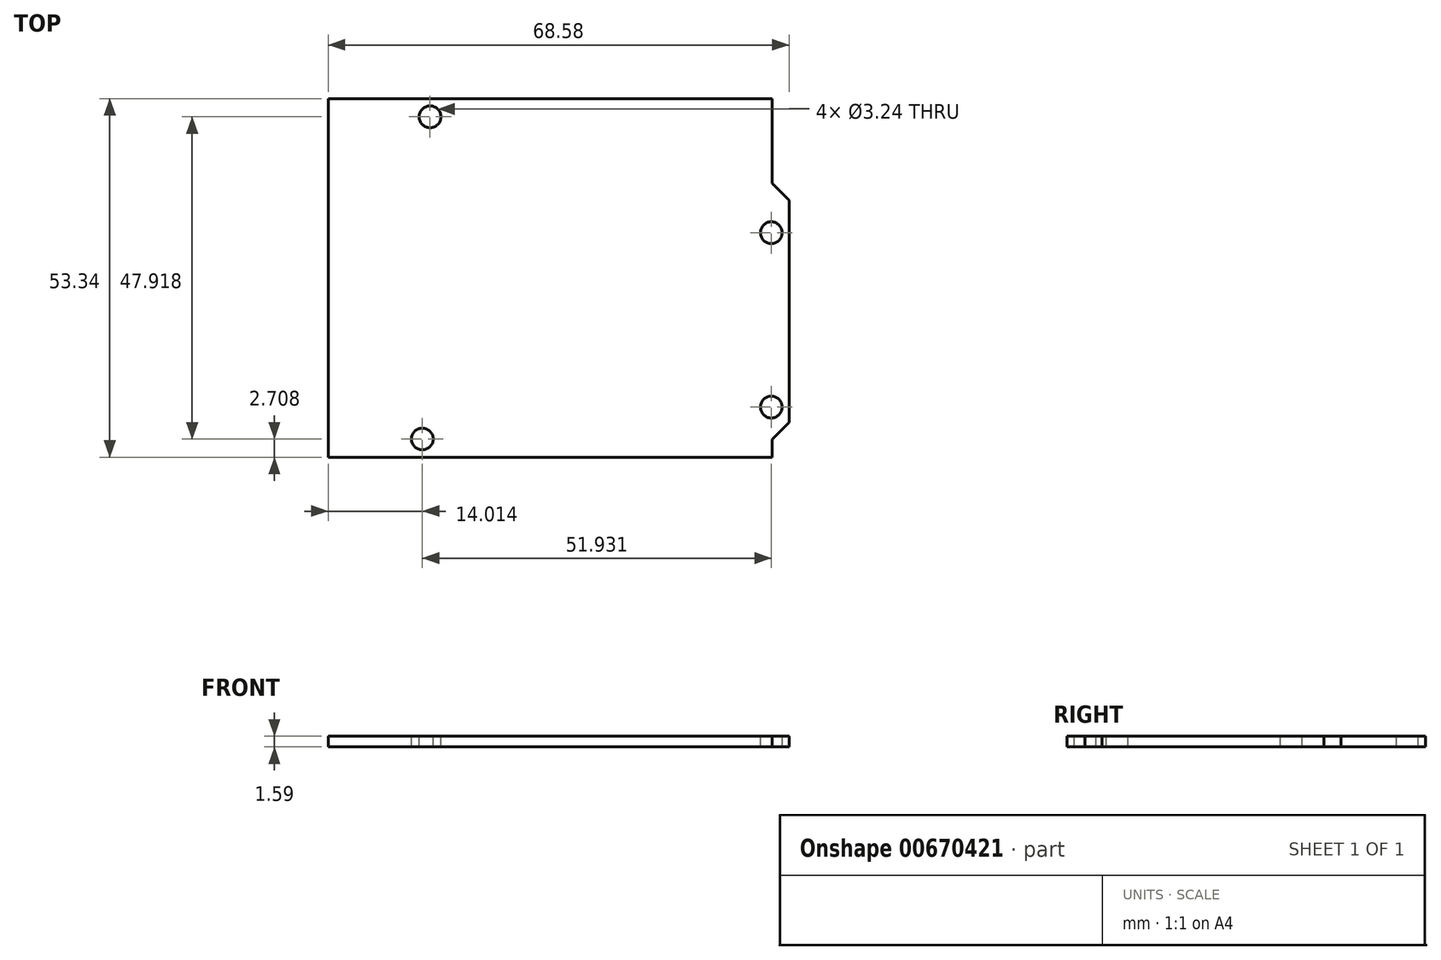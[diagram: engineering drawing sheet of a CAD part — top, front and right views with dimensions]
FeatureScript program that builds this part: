
annotation { "Feature Type Name" : "Feature", "Feature Type Description" : "" }
export const myFeature = defineFeature(function(context is Context, id is Id, definition is map)
    precondition{}
    {
        {
            var Q0;
            Q0=qCreatedBy(makeId("Top.planeOp"),FACE);
            var sketch = newSketch(context, id + "F0", { "sketchPlane" : qUnion([Q0])});
            skLineSegment(sketch, "E0", {"start": v(-33.02, 25.73) * mm, "end": v(33.02, 25.73) * mm});
            skLineSegment(sketch, "E1", {"start": v(33.02, 25.73) * mm, "end": v(33.02, 13.15) * mm});
            skLineSegment(sketch, "E2", {"start": v(33.02, -27.61) * mm, "end": v(-33.02, -27.61) * mm});
            skLineSegment(sketch, "E3", {"start": v(-33.02, -27.61) * mm, "end": v(-33.02, 25.73) * mm});
            skLineSegment(sketch, "E4", {"start": v(33.02, -24.95) * mm, "end": v(35.56, -22.4) * mm});
            skLineSegment(sketch, "E5", {"start": v(35.56, -22.4) * mm, "end": v(35.56, 10.61) * mm});
            skLineSegment(sketch, "E6", {"start": v(35.56, 10.61) * mm, "end": v(33.02, 13.15) * mm});
            skLineSegment(sketch, "E7", {"start": v(0, 25.73) * mm, "end": v(0, 0) * mm, "construction": true});
            skLineSegment(sketch, "E8", {"start": v(0, 0) * mm, "end": v(-33.02, 0) * mm, "construction": true});
            skLineSegment(sketch, "E9.trimOffspring", {"start": v(33.02, -24.95) * mm, "end": v(33.02, -27.61) * mm});
            skSolve(sketch);
        }
        {
            var Q0;
            Q0 = qSketchRegion(id + "F0", true);
            extrude(context, id + "F1", {"entities" : qUnion([Q0]), "depth" : 1.59 * mm, "offsetDistance" : 25 * mm});
        }
        {
            var Q0;
            Q0=makeQuery(id+"F1.opExtrude","CAP_FACE",FACE,{"disambiguationData":[OSD([sQuery(id+"F0.wireOp",EDGE,"E0"),sQuery(id+"F0.wireOp",EDGE,"E1"),sQuery(id+"F0.wireOp",EDGE,"E2"),sQuery(id+"F0.wireOp",EDGE,"E3"),sQuery(id+"F0.wireOp",EDGE,"E4"),sQuery(id+"F0.wireOp",EDGE,"E5"),sQuery(id+"F0.wireOp",EDGE,"E6"),sQuery(id+"F0.wireOp",EDGE,"E9.trimOffspring")])],"isStart":false});
            var sketch = newSketch(context, id + "F2", { "sketchPlane" : qUnion([Q0])});
            skCircle(sketch, "E10", {"center": v(-17.85, 23.02) * mm, "radius": 1.62 * mm});
            skCircle(sketch, "E11", {"center": v(32.92, 5.78) * mm, "radius": 1.62 * mm});
            skCircle(sketch, "E12", {"center": v(32.92, -20.15) * mm, "radius": 1.62 * mm});
            skCircle(sketch, "E13", {"center": v(-19, -24.9) * mm, "radius": 1.62 * mm});
            skSolve(sketch);
        }
        {
            var Q0;
            Q0 = qSketchRegion(id + "F2", true);
            extrude(context, id + "F3", {"entities" : qUnion([Q0]), "operationType" : NewBodyOperationType.REMOVE, "endBound" : BoundingType.THROUGH_ALL, "oppositeDirection" : true, "depth" : 25 * mm, "offsetDistance" : 25 * mm});
        }
    });
